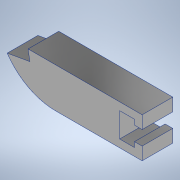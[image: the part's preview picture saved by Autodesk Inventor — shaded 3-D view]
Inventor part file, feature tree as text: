
AUTODESK INVENTOR PART (.ipt)
format: ipt  version: 2022 (Build 260153000, 153)  size: 151,040 bytes
history: native  units: mm
features: extrude x2, fillet x1, sketch x1
ambient origin geometry x8: Origin, YZ Plane, XZ Plane, XY Plane, X Axis, Y Axis, Z Axis, Center Point
bodies: Body1 (feature_tree)
feature tree (4):
  extrude  "Extrusion2"  Depth=23.0mm
  extrude  "Extrusion5"  Depth=3.0mm
  fillet  "Fillet2"  Radius=12.0mm
  sketch  "Sketch8"  dims[d41=5.8mm d48=44.0mm d50=3.0mm d56=12.0mm d57=0.0mm d63=45.0mm d67=15.6mm d71=0.0mm d80=17.453293mm d82=0.0mm d83=0.0mm d87=5.6mm d88=9.6mm d95=4.0mm d96=9.0mm d97=15.6mm d98=23.0mm]
